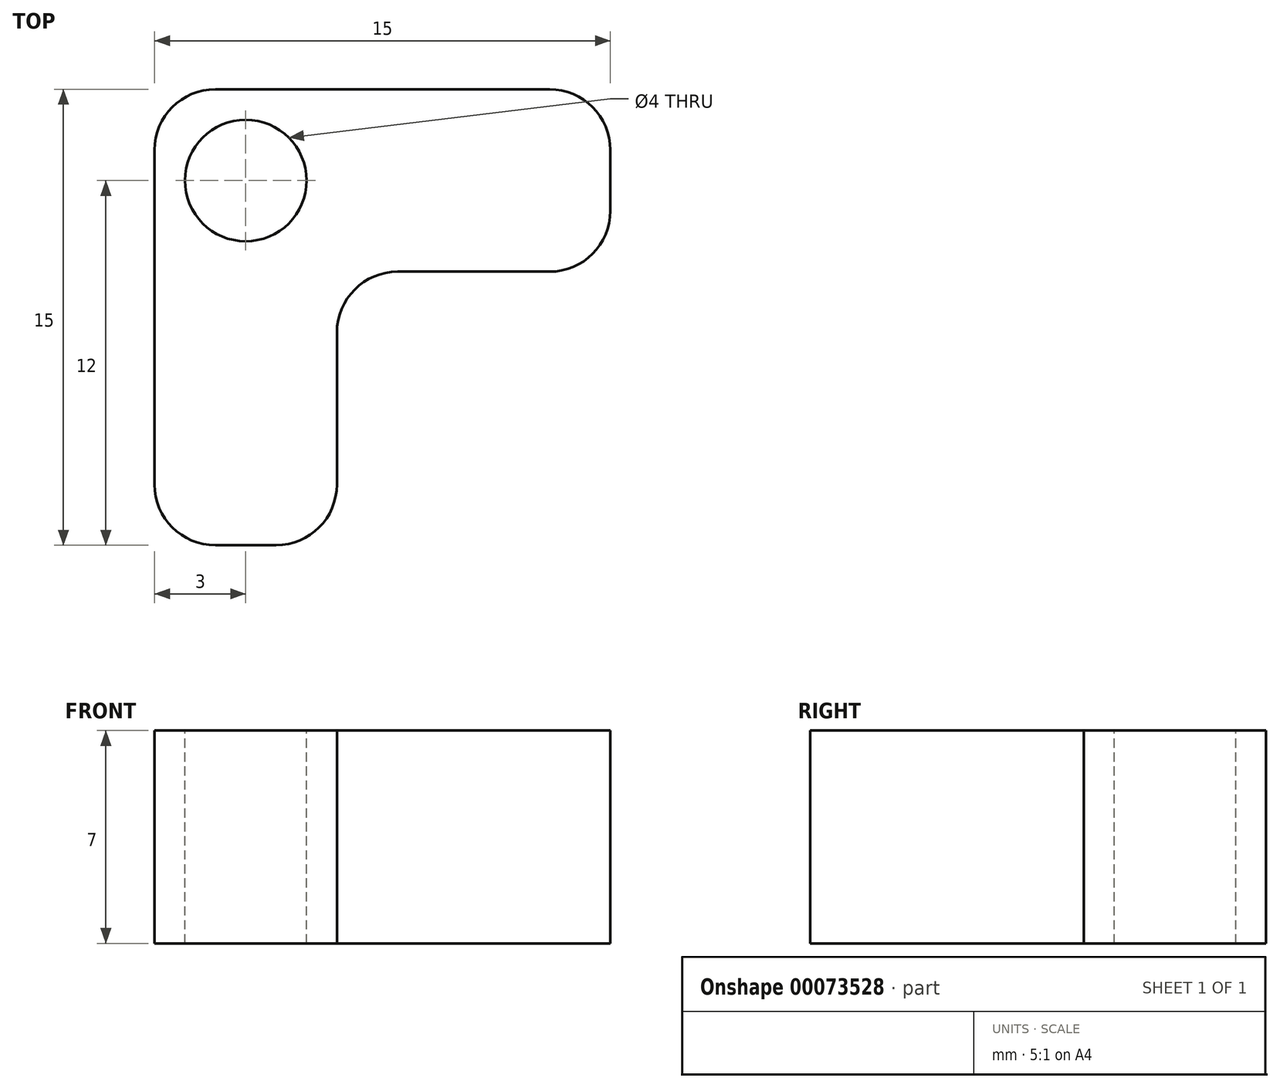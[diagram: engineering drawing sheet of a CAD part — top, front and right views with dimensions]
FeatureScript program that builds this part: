
annotation { "Feature Type Name" : "Feature", "Feature Type Description" : "" }
export const myFeature = defineFeature(function(context is Context, id is Id, definition is map)
    precondition{}
    {
        {
            var Q0;
            Q0=qCreatedBy(makeId("Top.planeOp"),FACE);
            var sketch = newSketch(context, id + "F0", { "sketchPlane" : qUnion([Q0])});
            skLineSegment(sketch, "E0", {"start": v(0, -15) * mm, "end": v(0, 0) * mm});
            skLineSegment(sketch, "E1", {"start": v(0, 0) * mm, "end": v(15, 0) * mm});
            skLineSegment(sketch, "E2", {"start": v(15, 0) * mm, "end": v(15, -6) * mm});
            skLineSegment(sketch, "E3", {"start": v(15, -6) * mm, "end": v(8, -6) * mm});
            skLineSegment(sketch, "E4", {"start": v(6, -8) * mm, "end": v(6, -15) * mm});
            skLineSegment(sketch, "E5", {"start": v(6, -15) * mm, "end": v(0, -15) * mm});
            skPoint(sketch, "E6.visualSharp", {"position": v(6, -6) * mm});
            skArc(sketch, "E6.filletArc", {"start": v(8, -6) * mm, "mid": v(6.59, -6.59) * mm, "end": v(6, -8) * mm});
            skSolve(sketch);
        }
        {
            var Q0;
            Q0=makeQuery(id+"F0.imprint","IMPRINT",FACE,{"disambiguationData":[TD([[makeQuery(id+"F0.imprint","IMPRINT",EDGE,{"derivedFrom":sQuery(id+"F0.wireOp",EDGE,"E0")}),-1.0]])]});
            extrude(context, id + "F1", {"entities" : qUnion([Q0]), "depth" : 7 * mm});
        }
        {
            var Q0;
            Q0=makeQuery(id+"F1.opExtrude","CAP_FACE",FACE,{"disambiguationData":[OSD([sQuery(id+"F0.wireOp",EDGE,"E0"),sQuery(id+"F0.wireOp",EDGE,"E1"),sQuery(id+"F0.wireOp",EDGE,"E2"),sQuery(id+"F0.wireOp",EDGE,"E3"),sQuery(id+"F0.wireOp",EDGE,"E4"),sQuery(id+"F0.wireOp",EDGE,"E5"),sQuery(id+"F0.wireOp",EDGE,"E6.filletArc")])],"isStart":false});
            var sketch = newSketch(context, id + "F2", { "sketchPlane" : qUnion([Q0])});
            skLineSegment(sketch, "E7", {"start": v(0, 0) * mm, "end": v(6.59, -6.59) * mm, "construction": true});
            skLineSegment(sketch, "E8", {"start": v(15, -3) * mm, "end": v(3, -3) * mm, "construction": true});
            skLineSegment(sketch, "E9", {"start": v(3, -3) * mm, "end": v(3, -15) * mm, "construction": true});
            skCircle(sketch, "E10", {"center": v(3, -3) * mm, "radius": 2 * mm});
            skSolve(sketch);
        }
        {
            var Q0;
            Q0=sQuery(id+"F2.wireOp",VERTEX,"E10.center");
            var Q1;
            Q1=makeQuery(id+"F1.opExtrude","SWEPT_BODY",BODY,{"disambiguationData":[OSD([sQuery(id+"F0.wireOp",EDGE,"E0"),sQuery(id+"F0.wireOp",EDGE,"E1"),sQuery(id+"F0.wireOp",EDGE,"E2"),sQuery(id+"F0.wireOp",EDGE,"E3"),sQuery(id+"F0.wireOp",EDGE,"E4"),sQuery(id+"F0.wireOp",EDGE,"E5"),sQuery(id+"F0.wireOp",EDGE,"E6.filletArc")])]});
            hole(context, id + "F3", {"style" : HoleStyle.SIMPLE, "holeDiameter" : 4 * mm, "endStyle" : HoleEndStyle.THROUGH, "locations" : qUnion([Q0]), "scope" : qUnion([Q1])});
        }
        {
            var Q0;
            Q0=makeQuery(id+"F1.opExtrude","SWEPT_EDGE",EDGE,{"disambiguationData":[OSD([sQuery(id+"F0.wireOp",EDGE,"E0"),sQuery(id+"F0.wireOp",EDGE,"E1")])]});
            var Q1;
            Q1=makeQuery(id+"F1.opExtrude","SWEPT_EDGE",EDGE,{"disambiguationData":[OSD([sQuery(id+"F0.wireOp",EDGE,"E0"),sQuery(id+"F0.wireOp",EDGE,"E5")])]});
            var Q2;
            Q2=makeQuery(id+"F1.opExtrude","SWEPT_EDGE",EDGE,{"disambiguationData":[OSD([sQuery(id+"F0.wireOp",EDGE,"E4"),sQuery(id+"F0.wireOp",EDGE,"E5")])]});
            var Q3;
            Q3=makeQuery(id+"F1.opExtrude","SWEPT_EDGE",EDGE,{"disambiguationData":[OSD([sQuery(id+"F0.wireOp",EDGE,"E2"),sQuery(id+"F0.wireOp",EDGE,"E3")])]});
            var Q4;
            Q4=makeQuery(id+"F1.opExtrude","SWEPT_EDGE",EDGE,{"disambiguationData":[OSD([sQuery(id+"F0.wireOp",EDGE,"E1"),sQuery(id+"F0.wireOp",EDGE,"E2")])]});
            fillet(context, id + "F4", {"entities" : qUnion([Q0, Q1, Q2, Q3, Q4]), "radius" : 2 * mm, "allowEdgeOverflow" : false});
        }
    });
